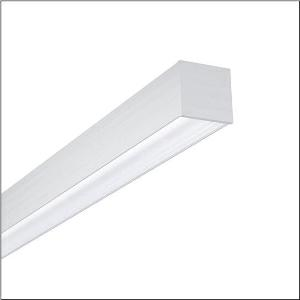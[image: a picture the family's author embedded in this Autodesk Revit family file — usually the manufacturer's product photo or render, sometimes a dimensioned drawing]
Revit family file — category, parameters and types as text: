
# Revit family: silica_r_5mx21bd1e4a_4ae4
name_source: partatom
category: Lighting Fixtures
units: mm (PartAtom-declared; Revit-internal decimal feet)

## family parameters
Cut with Voids When Loaded = No
Host = Face
Light Source = No
Part Type = Normal
Room Calculation Point = No
Round Connector Dimension = Use Diameter
Shared = No

## types (1)
- --- (1 x LED, 4950 lm, 29.3 W, 4000K)
    Apparent Load = 29 VA
    CIE Flux Codes = 82 97 100 100 100
    Color Rendering = 80
    Color Temperature = 4000K
    Default Elevation = 1800 mm
    Description = Silica®, office luminaire, of aluminium, light emission: direct distribution, primary light characteristic: symmetric, installation type: surface-mounted, LED, rated luminous flux: 4.950lm, luminous efficacy: 169lm/W, light colour: 840, colour temperature: 4000K, control gear: ECG DALI, with terminal, 3+2-pole, max. 2.5mm², mains connection: 230V, AC, 50/60Hz, rated input power: 29W, luminaire housing, of aluminium, anodised, silver, length: 1.442mm, width: 65mm, height: 64mm, protection rating (complete): IP20, insulation class (complete): insulation class I (protective earthing), certification: CE, permissible operating ambient temperature: 0..+35°C, standard: EN 50419, packaging unit: 1 piece
    Height = 64 mm
    Lamp = 1 x LED
    Lamp Light Flux = 4950 lm
    Lamp Power = 29.3 W
    Lamp count = 1
    Length = 1442 mm
    Luminous efficacy = 169 lm/W
    Manufacturer = Siteco
    ModVariant = No
    Model = 5MX21BD1E4A
    Mounting Place = Ceiling
    Mounting Type = Surface mounted
    Number of Poles = 1
    OnlyDefault = Yes
    Power Factor = 1
    Product Name = Silica®
    Product group = office luminaire | ceiling mounted
    ProductGroupID = 300
    Protection Class = Protection class I
    Protection Degree = IP 20
    RLX_Detail_Level = 1
    RLX_Emergency_Light_Flux = 0 lm
    RLX_Emergency_Type = 0
    RLX_Emergency_Type_DB = No
    RlxData = <blob elided: 27265 chars, md5=d451d390>
    Socket = socket
    Standby Power = 0 W
    System Light Flux = 4950 lm
    System Power = 29 W
    Type Comments = factory setting: luminous flux: 100 % | dim-lin: 254 | 163 mA
    Type Image = l_1004827.jpg
    URL = http://relux.com
    VarID = @adj_155550
    Voltage = 0 V
    Weight = 0.00 kg
    Width = 66 mm

## geometry (parser evidence)
native form markers: Blend x4, Sweep x11
no freeform markers — native parametric forms only
